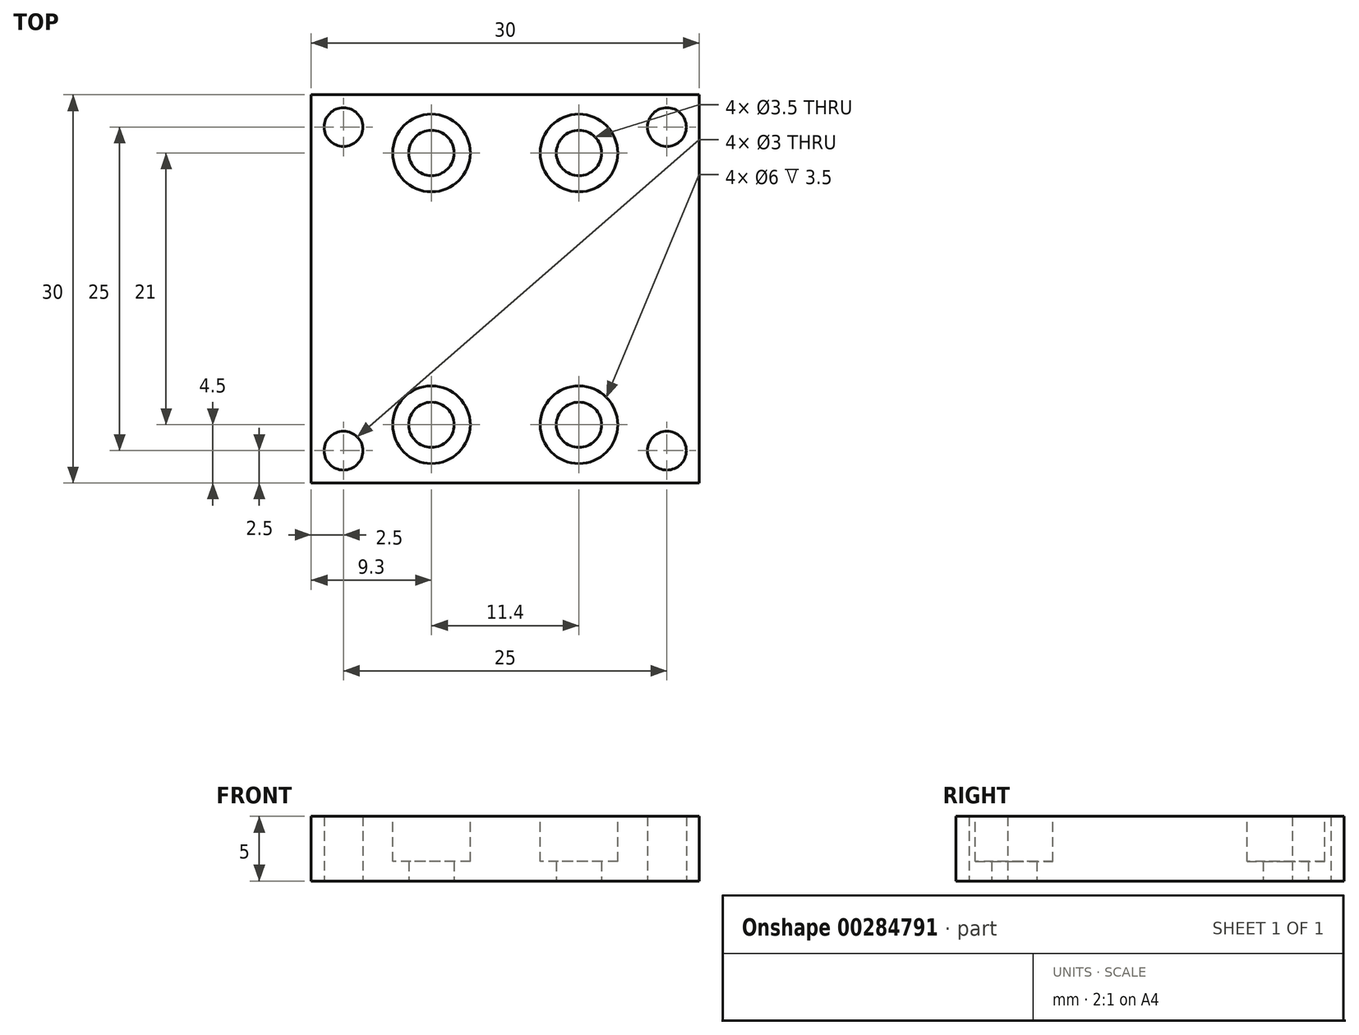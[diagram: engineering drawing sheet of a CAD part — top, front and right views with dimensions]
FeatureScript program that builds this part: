
annotation { "Feature Type Name" : "Feature", "Feature Type Description" : "" }
export const myFeature = defineFeature(function(context is Context, id is Id, definition is map)
    precondition{}
    {
        {
            var Q0;
            Q0=qCreatedBy(makeId("Top.planeOp"),FACE);
            var sketch = newSketch(context, id + "F0", { "sketchPlane" : qUnion([Q0])});
            skLineSegment(sketch, "E0.bottom", {"start": v(-15, 15) * mm, "end": v(15, 15) * mm});
            skLineSegment(sketch, "E0.top", {"start": v(-15, -15) * mm, "end": v(15, -15) * mm});
            skLineSegment(sketch, "E0.left", {"start": v(-15, 15) * mm, "end": v(-15, -15) * mm});
            skLineSegment(sketch, "E0.right", {"start": v(15, 15) * mm, "end": v(15, -15) * mm});
            skCircle(sketch, "E1", {"center": v(-12.5, 12.5) * mm, "radius": 1.5 * mm});
            skCircle(sketch, "E2", {"center": v(12.5, 12.5) * mm, "radius": 1.5 * mm});
            skCircle(sketch, "E3", {"center": v(-12.5, -12.5) * mm, "radius": 1.5 * mm});
            skCircle(sketch, "E4", {"center": v(12.5, -12.5) * mm, "radius": 1.5 * mm});
            skCircle(sketch, "E5", {"center": v(-5.7, 10.5) * mm, "radius": 1.75 * mm});
            skCircle(sketch, "E6", {"center": v(5.7, 10.5) * mm, "radius": 1.75 * mm});
            skCircle(sketch, "E7", {"center": v(-5.7, -10.5) * mm, "radius": 1.75 * mm});
            skCircle(sketch, "E8", {"center": v(5.7, -10.5) * mm, "radius": 1.75 * mm});
            skSolve(sketch);
        }
        {
            var Q0;
            Q0 = qSketchRegion(id + "F0", true);
            extrude(context, id + "F1", {"entities" : qUnion([Q0]), "depth" : 5 * mm});
        }
        {
            var Q0;
            Q0=makeQuery(id+"F1.opExtrude","CAP_FACE",FACE,{"disambiguationData":[OSD([sQuery(id+"F0.wireOp",EDGE,"E0.bottom"),sQuery(id+"F0.wireOp",EDGE,"E0.top"),sQuery(id+"F0.wireOp",EDGE,"E0.left"),sQuery(id+"F0.wireOp",EDGE,"E0.right"),sQuery(id+"F0.wireOp",EDGE,"E1"),sQuery(id+"F0.wireOp",EDGE,"E2"),sQuery(id+"F0.wireOp",EDGE,"E3"),sQuery(id+"F0.wireOp",EDGE,"E4"),sQuery(id+"F0.wireOp",EDGE,"E5"),sQuery(id+"F0.wireOp",EDGE,"E6"),sQuery(id+"F0.wireOp",EDGE,"E7"),sQuery(id+"F0.wireOp",EDGE,"E8")])],"isStart":false});
            var sketch = newSketch(context, id + "F2", { "sketchPlane" : qUnion([Q0])});
            skCircle(sketch, "E9", {"center": v(-5.7, 10.5) * mm, "radius": 3 * mm});
            skCircle(sketch, "E10", {"center": v(5.7, 10.5) * mm, "radius": 3 * mm});
            skCircle(sketch, "E11", {"center": v(5.7, -10.5) * mm, "radius": 3 * mm});
            skCircle(sketch, "E12", {"center": v(-5.7, -10.5) * mm, "radius": 3 * mm});
            skSolve(sketch);
        }
        {
            var Q0;
            Q0 = qSketchRegion(id + "F2", true);
            extrude(context, id + "F3", {"entities" : qUnion([Q0]), "operationType" : NewBodyOperationType.REMOVE, "oppositeDirection" : true, "depth" : 3.5 * mm});
        }
    });
